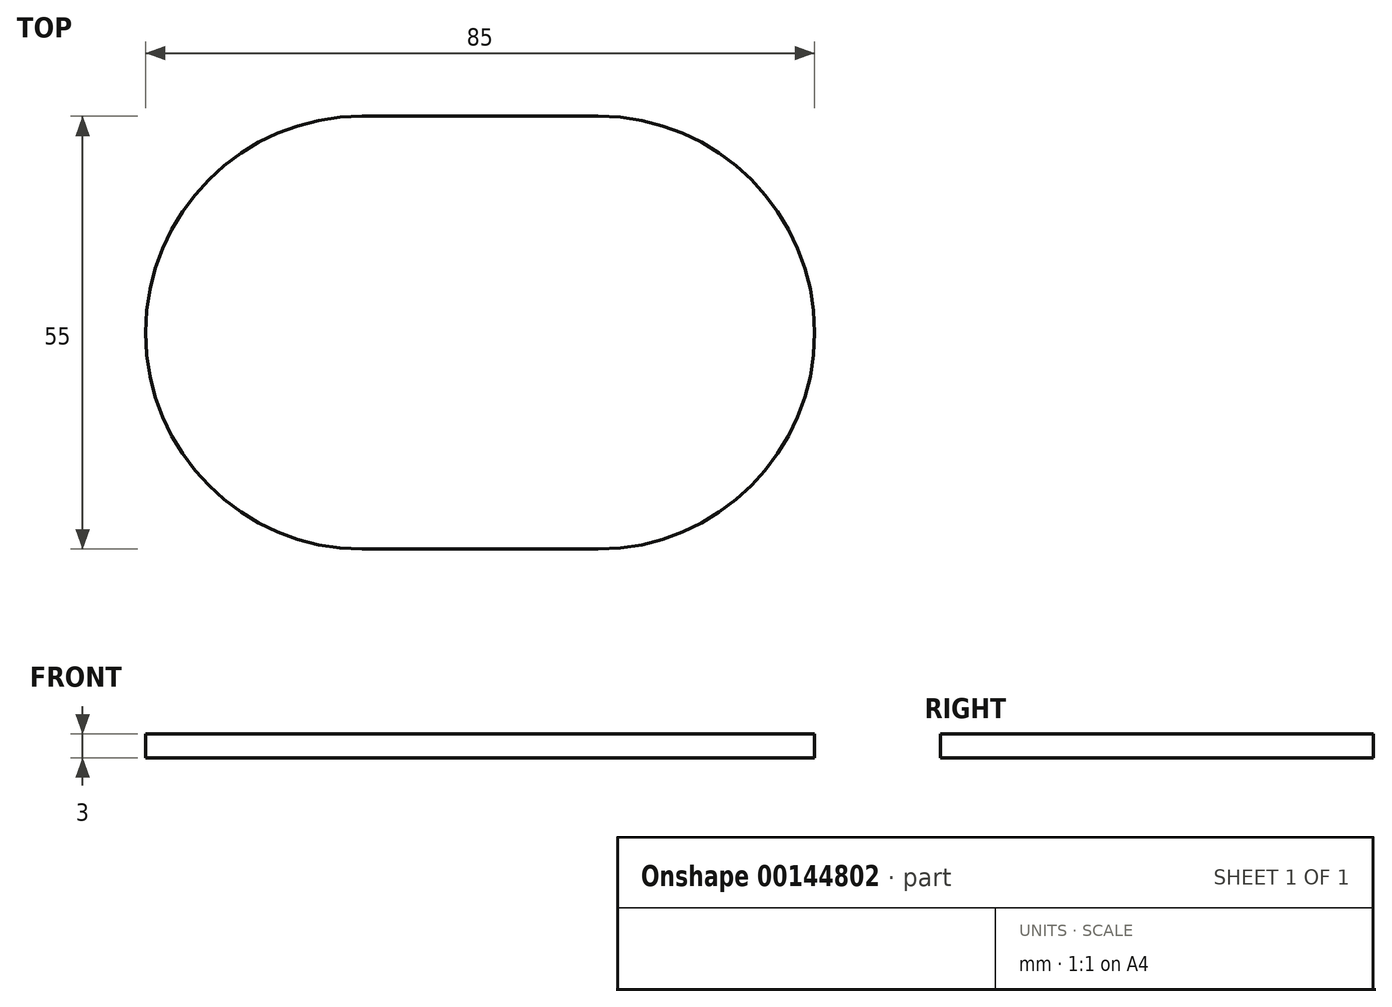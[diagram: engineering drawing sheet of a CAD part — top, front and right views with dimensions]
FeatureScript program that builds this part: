
annotation { "Feature Type Name" : "Feature", "Feature Type Description" : "" }
export const myFeature = defineFeature(function(context is Context, id is Id, definition is map)
    precondition{}
    {
        {
            var Q0;
            Q0=qCreatedBy(makeId("Top.planeOp"),FACE);
            var sketch = newSketch(context, id + "F0", { "sketchPlane" : qUnion([Q0])});
            skLineSegment(sketch, "E0.bottom", {"start": v(-15, 28.47) * mm, "end": v(0, 28.47) * mm});
            skLineSegment(sketch, "E0.top", {"start": v(-15, -26.53) * mm, "end": v(0, -26.53) * mm});
            skPoint(sketch, "E0.middle", {"position": v(0, 0) * mm});
            skArc(sketch, "E1", {"start": v(-15, 28.47) * mm, "mid": v(-42.5, 0.97) * mm, "end": v(-15, -26.53) * mm});
            skLineSegment(sketch, "E2.MirrorCS", {"start": v(15, 28.47) * mm, "end": v(0, 28.47) * mm});
            skArc(sketch, "E3.MirrorCS", {"start": v(15, 28.47) * mm, "mid": v(42.5, 0.97) * mm, "end": v(15, -26.53) * mm});
            skLineSegment(sketch, "E4.MirrorCS", {"start": v(15, -26.53) * mm, "end": v(0, -26.53) * mm});
            skSolve(sketch);
        }
        {
            var Q0;
            Q0=makeQuery(id+"F0.imprint","IMPRINT",FACE,{"disambiguationData":[TD([[makeQuery(id+"F0.imprint","IMPRINT",EDGE,{"derivedFrom":sQuery(id+"F0.wireOp",EDGE,"E0.bottom")}),-1.0]])]});
            extrude(context, id + "F1", {"entities" : qUnion([Q0]), "depth" : 3 * mm});
        }
    });
